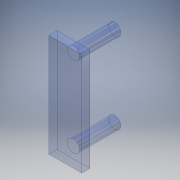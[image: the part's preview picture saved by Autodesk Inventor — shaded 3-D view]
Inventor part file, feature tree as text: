
AUTODESK INVENTOR PART (.ipt)
format: ipt  version: 2018 (Build 220112000, 112)  size: 219,136 bytes
history: native  units: mm
features: extrude x2, sketch x1
ambient origin geometry x8: Origin, YZ Plane, XZ Plane, XY Plane, X Axis, Y Axis, Z Axis, Center Point
bodies: 实体1 (feature_tree)
feature tree (3):
  sketch  "草图1"  dims[d0=25.0mm d1=8.0mm d2=3.0mm d6=19.57mm d7=10.0mm d8=0.0mm d9=2.0mm d10=0.0mm]
  extrude  "拉伸1"  Depth=8.0mm
  extrude  "拉伸2"  Depth=2.0mm
